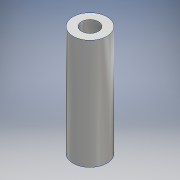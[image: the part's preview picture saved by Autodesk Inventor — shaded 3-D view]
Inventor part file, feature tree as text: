
AUTODESK INVENTOR PART (.ipt)
format: ipt  version: 2016 (Build 200138000, 138)  size: 112,128 bytes
history: native  units: mm
features: other x3, sketch x3, extrude x3, hole x2
ambient origin geometry x8: Origin, YZ Plane, XZ Plane, XY Plane, X Axis, Y Axis, Z Axis, Center Point
bodies: Body1 (feature_tree)
feature tree (11):
  other  "ソリッド1"
  sketch  "スケッチ1"
  extrude  "押し出し1"  Depth=8.0mm
  sketch  "スケッチ2"
  extrude  "押し出し2"  Depth=4.001mm
  hole  "穴1"  [1 undecoded]
  hole  "穴2"  [1 undecoded]
  other  "作業平面1"
  extrude  "押し出し3"  Depth=25.0mm TaperAngle=0.0deg
  sketch  "スケッチ3"
  other  "断面エッジを投影1"
note: 2 required parameter values undecoded (feature->parameter linkage not recoverable at this tier; creation-order binding heuristic only, values carry confidence <= 0.55)
